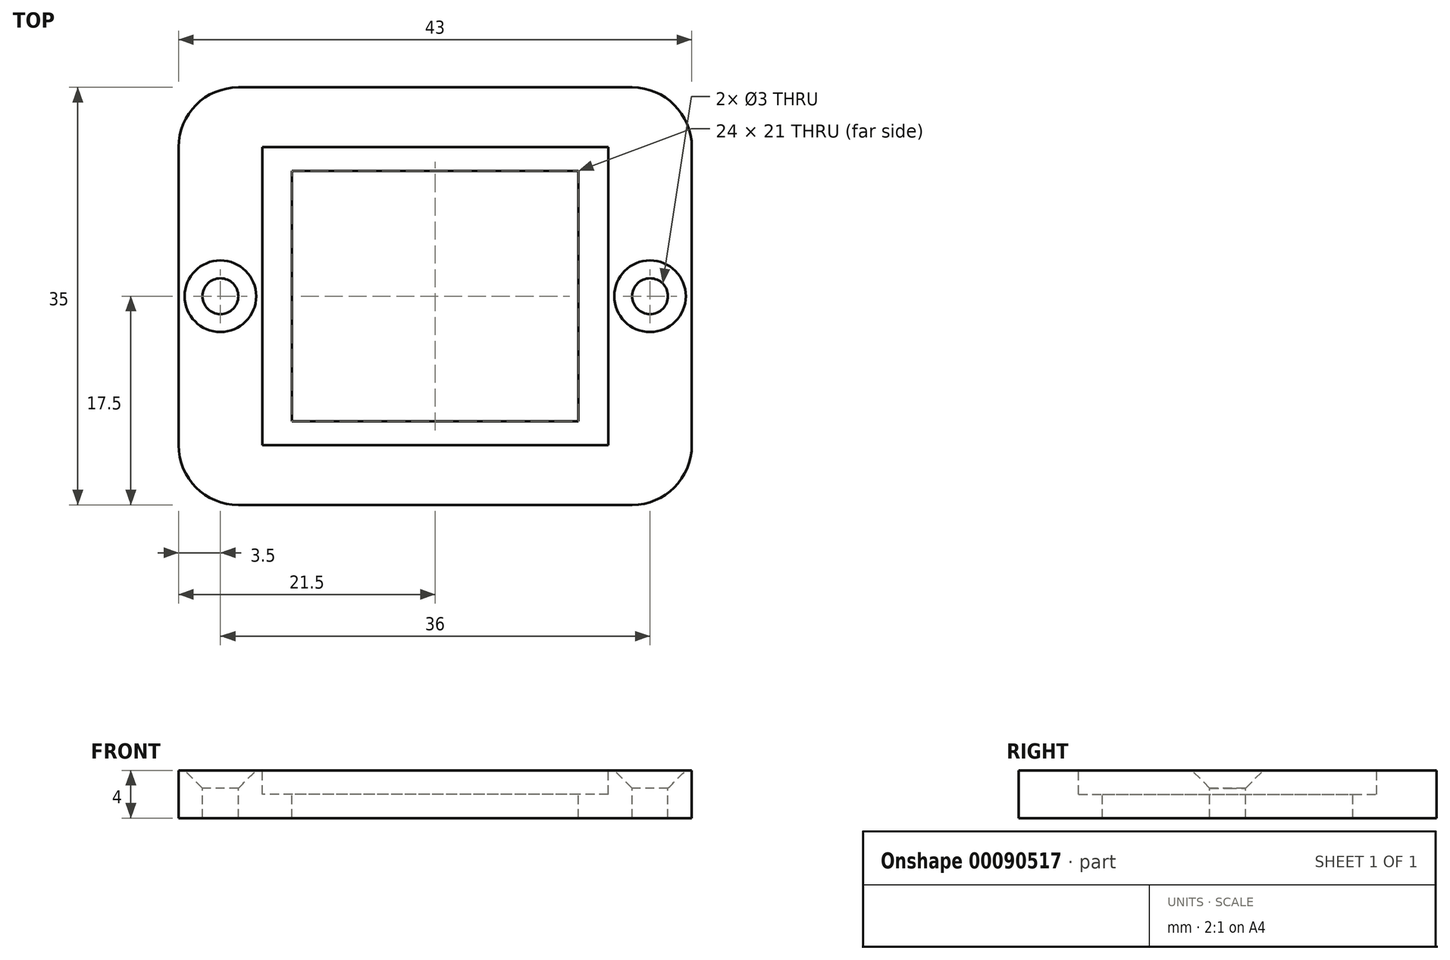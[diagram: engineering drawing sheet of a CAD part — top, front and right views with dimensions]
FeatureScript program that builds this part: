
annotation { "Feature Type Name" : "Feature", "Feature Type Description" : "" }
export const myFeature = defineFeature(function(context is Context, id is Id, definition is map)
    precondition{}
    {
        {
            var Q0;
            Q0=qCreatedBy(makeId("Top.planeOp"),FACE);
            var sketch = newSketch(context, id + "F0", { "sketchPlane" : qUnion([Q0])});
            skLineSegment(sketch, "E0.bottom", {"start": v(16.5, -17.5) * mm, "end": v(-16.5, -17.5) * mm});
            skLineSegment(sketch, "E0.top", {"start": v(16.5, 17.5) * mm, "end": v(-16.5, 17.5) * mm});
            skLineSegment(sketch, "E0.left", {"start": v(21.5, -12.5) * mm, "end": v(21.5, 12.5) * mm});
            skLineSegment(sketch, "E0.right", {"start": v(-21.5, -12.5) * mm, "end": v(-21.5, 12.5) * mm});
            skPoint(sketch, "E0.middle", {"position": v(0, 0) * mm});
            skPoint(sketch, "E1.visualSharp", {"position": v(-21.5, 17.5) * mm});
            skArc(sketch, "E1.filletArc", {"start": v(-16.5, 17.5) * mm, "mid": v(-20.04, 16.04) * mm, "end": v(-21.5, 12.5) * mm});
            skPoint(sketch, "E2.visualSharp", {"position": v(21.5, 17.5) * mm});
            skArc(sketch, "E2.filletArc", {"start": v(21.5, 12.5) * mm, "mid": v(20.04, 16.04) * mm, "end": v(16.5, 17.5) * mm});
            skPoint(sketch, "E3.visualSharp", {"position": v(21.5, -17.5) * mm});
            skArc(sketch, "E3.filletArc", {"start": v(16.5, -17.5) * mm, "mid": v(20.04, -16.04) * mm, "end": v(21.5, -12.5) * mm});
            skPoint(sketch, "E4.visualSharp", {"position": v(-21.5, -17.5) * mm});
            skArc(sketch, "E4.filletArc", {"start": v(-21.5, -12.5) * mm, "mid": v(-20.04, -16.04) * mm, "end": v(-16.5, -17.5) * mm});
            skSolve(sketch);
        }
        {
            var Q0;
            Q0=makeQuery(id+"F0.imprint","IMPRINT",FACE,{"disambiguationData":[TD([[makeQuery(id+"F0.imprint","IMPRINT",EDGE,{"derivedFrom":sQuery(id+"F0.wireOp",EDGE,"E0.bottom")}),-1.0]])]});
            extrude(context, id + "F1", {"entities" : qUnion([Q0]), "depth" : 4 * mm});
        }
        {
            var Q0;
            Q0=makeQuery(id+"F1.opExtrude","CAP_FACE",FACE,{"disambiguationData":[OSD([sQuery(id+"F0.wireOp",EDGE,"E0.bottom"),sQuery(id+"F0.wireOp",EDGE,"E0.top"),sQuery(id+"F0.wireOp",EDGE,"E0.left"),sQuery(id+"F0.wireOp",EDGE,"E0.right")])],"isStart":false});
            var sketch = newSketch(context, id + "F2", { "sketchPlane" : qUnion([Q0])});
            skLineSegment(sketch, "E5.bottom", {"start": v(14.5, -12.5) * mm, "end": v(-14.5, -12.5) * mm});
            skLineSegment(sketch, "E5.top", {"start": v(14.5, 12.5) * mm, "end": v(-14.5, 12.5) * mm});
            skLineSegment(sketch, "E5.left", {"start": v(14.5, -12.5) * mm, "end": v(14.5, 12.5) * mm});
            skLineSegment(sketch, "E5.right", {"start": v(-14.5, -12.5) * mm, "end": v(-14.5, 12.5) * mm});
            skPoint(sketch, "E5.middle", {"position": v(0, 0) * mm});
            skSolve(sketch);
        }
        {
            var Q0;
            Q0 = qSketchRegion(id + "F2", true);
            extrude(context, id + "F3", {"entities" : qUnion([Q0]), "operationType" : NewBodyOperationType.REMOVE, "oppositeDirection" : true, "depth" : 2 * mm});
        }
        {
            var Q0;
            Q0=makeQuery(id+"F3.boolean.opBoolean","COPY",FACE,{"derivedFrom":makeQuery(id+"F3.opExtrude","CAP_FACE",FACE,{"disambiguationData":[OSD([sQuery(id+"F2.wireOp",EDGE,"E5.bottom"),sQuery(id+"F2.wireOp",EDGE,"E5.top"),sQuery(id+"F2.wireOp",EDGE,"E5.left"),sQuery(id+"F2.wireOp",EDGE,"E5.right")])],"isStart":false})});
            var sketch = newSketch(context, id + "F4", { "sketchPlane" : qUnion([Q0])});
            skLineSegment(sketch, "E6.bottom", {"start": v(12, -10.5) * mm, "end": v(-12, -10.5) * mm});
            skLineSegment(sketch, "E6.top", {"start": v(12, 10.5) * mm, "end": v(-12, 10.5) * mm});
            skLineSegment(sketch, "E6.left", {"start": v(12, -10.5) * mm, "end": v(12, 10.5) * mm});
            skLineSegment(sketch, "E6.right", {"start": v(-12, -10.5) * mm, "end": v(-12, 10.5) * mm});
            skPoint(sketch, "E6.middle", {"position": v(0, 0) * mm});
            skSolve(sketch);
        }
        {
            var Q0;
            Q0 = qSketchRegion(id + "F4", true);
            extrude(context, id + "F5", {"entities" : qUnion([Q0]), "operationType" : NewBodyOperationType.REMOVE, "oppositeDirection" : true, "depth" : 2 * mm});
        }
        {
            var Q0;
            Q0=makeQuery(id+"F1.opExtrude","CAP_FACE",FACE,{"disambiguationData":[OSD([sQuery(id+"F0.wireOp",EDGE,"E0.bottom"),sQuery(id+"F0.wireOp",EDGE,"E0.top"),sQuery(id+"F0.wireOp",EDGE,"E0.left"),sQuery(id+"F0.wireOp",EDGE,"E0.right")])],"isStart":false});
            var sketch = newSketch(context, id + "F6", { "sketchPlane" : qUnion([Q0])});
            skPoint(sketch, "E7", {"position": v(-18, 0) * mm});
            skPoint(sketch, "E8", {"position": v(18, 0) * mm});
            skSolve(sketch);
        }
        {
            var Q0;
            Q0=sQuery(id+"F6.wireOp",VERTEX,"E7");
            var Q1;
            Q1=makeQuery(id+"F1.opExtrude","SWEPT_BODY",BODY,{"disambiguationData":[OSD([sQuery(id+"F0.wireOp",EDGE,"E0.bottom"),sQuery(id+"F0.wireOp",EDGE,"E0.top"),sQuery(id+"F0.wireOp",EDGE,"E0.left"),sQuery(id+"F0.wireOp",EDGE,"E0.right")])]});
            hole(context, id + "F7", {"style" : HoleStyle.C_SINK, "endStyle" : HoleEndStyle.THROUGH, "holeDiameter" : 3 * mm, "cSinkDiameter" : 6 * mm, "cSinkAngle" : 90 * degree, "startFromSketch" : true, "locations" : qUnion([Q0]), "scope" : qUnion([Q1]), "isTappedThrough" : true});
        }
        {
            var Q0;
            Q0=sQuery(id+"F6.wireOp",VERTEX,"E8");
            var Q1;
            Q1=makeQuery(id+"F1.opExtrude","SWEPT_BODY",BODY,{"disambiguationData":[OSD([sQuery(id+"F0.wireOp",EDGE,"E0.bottom"),sQuery(id+"F0.wireOp",EDGE,"E0.top"),sQuery(id+"F0.wireOp",EDGE,"E0.left"),sQuery(id+"F0.wireOp",EDGE,"E0.right")])]});
            hole(context, id + "F8", {"style" : HoleStyle.C_SINK, "endStyle" : HoleEndStyle.THROUGH, "holeDiameter" : 3 * mm, "cSinkDiameter" : 6 * mm, "cSinkAngle" : 90 * degree, "startFromSketch" : true, "locations" : qUnion([Q0]), "scope" : qUnion([Q1]), "isTappedThrough" : true});
        }
    });
